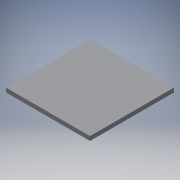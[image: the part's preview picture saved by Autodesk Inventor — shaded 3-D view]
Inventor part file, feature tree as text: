
AUTODESK INVENTOR PART (.ipt)
format: ipt  version: 2018.3 (Build 223284000, 284)  size: 81,920 bytes
history: native  units: mm
features: extrude x1, sketch x1
ambient origin geometry x8: Origin, YZ Plane, XZ Plane, XY Plane, X Axis, Y Axis, Z Axis, Center Point
bodies: Solid1 (feature_tree)
feature tree (2):
  extrude  "Extrusion1"  Depth=40.0mm
  sketch  "Sketch1"  dims[d0=40.0mm d1=40.0mm d2=2.0mm d3=0.0mm]
